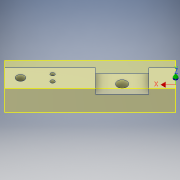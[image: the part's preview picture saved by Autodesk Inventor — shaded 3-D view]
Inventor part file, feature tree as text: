
AUTODESK INVENTOR PART (.ipt)
format: ipt  version: 2018 (Build 220112000, 112)  size: 481,280 bytes
history: native  units: in
note: dims shown in document units (in); Inventor stores cm internally (conversion verified against a paired STEP export)
features: sketch x8, extrude x7, other x1, hole x1, thread x1
ambient origin geometry x8: Origin, YZ Plane, XZ Plane, XY Plane, X Axis, Y Axis, Z Axis, Center Point
bodies: Solid1 (feature_tree)
feature tree (18):
  other  "Standard"
  extrude  "Extrusion1"  Depth=4.0in
  extrude  "Extrusion3"  Depth=1.25in
  extrude  "Extrusion4"  Depth=0.74in
  extrude  "Extrusion5"  Depth=0.187in
  extrude  "Extrusion6"  Depth=0.37in
  extrude  "Extrusion7"  Depth=0.25in
  extrude  "Extrusion8"  Depth=0.37in
  hole  "Hole1"  [1 undecoded]
  thread  "Thread1"  [1 undecoded]
  sketch  "Sketch1"  dims[d0=0.74in d1=4.0in]
  sketch  "Sketch2"  dims[d2=0.74in d3=0.0in d4=1.25in]
  sketch  "Sketch3"  dims[d5=0.625in d6=0.74in]
  sketch  "Sketch4"  dims[d9=0.187in d10=0.0in d11=0.312in]
  sketch  "Sketch5"  dims[d12=0.625in d13=0.37in]
  sketch  "Sketch6"  dims[d14=0.6in d15=0.0in d16=0.25in]
  sketch  "Sketch7"  dims[d17=0.375in d18=0.37in]
  sketch  "Sketch9"  dims[d19=0.8in d20=0.0in d21=0.125in d22=0.125in d23=1.125in d24=1.125in d25=0.0687in d26=0.0687in d27=0.8in d28=0.0in d29=0.125in d31=0.0687in d32=1.125in d33=0.437in d34=0.0in d35=0.125in d36=0.365in d37=1.125in d38=0.3in d39=0.0in d43=0.25in d44=0.75in d45=0.375in d46=0.25in d47=0.5635in d48=0.75in d49=0.8108in d50=1.0in d51=0.0in]
note: 2 required parameter values undecoded (feature->parameter linkage not recoverable at this tier; creation-order binding heuristic only, values carry confidence <= 0.55)
